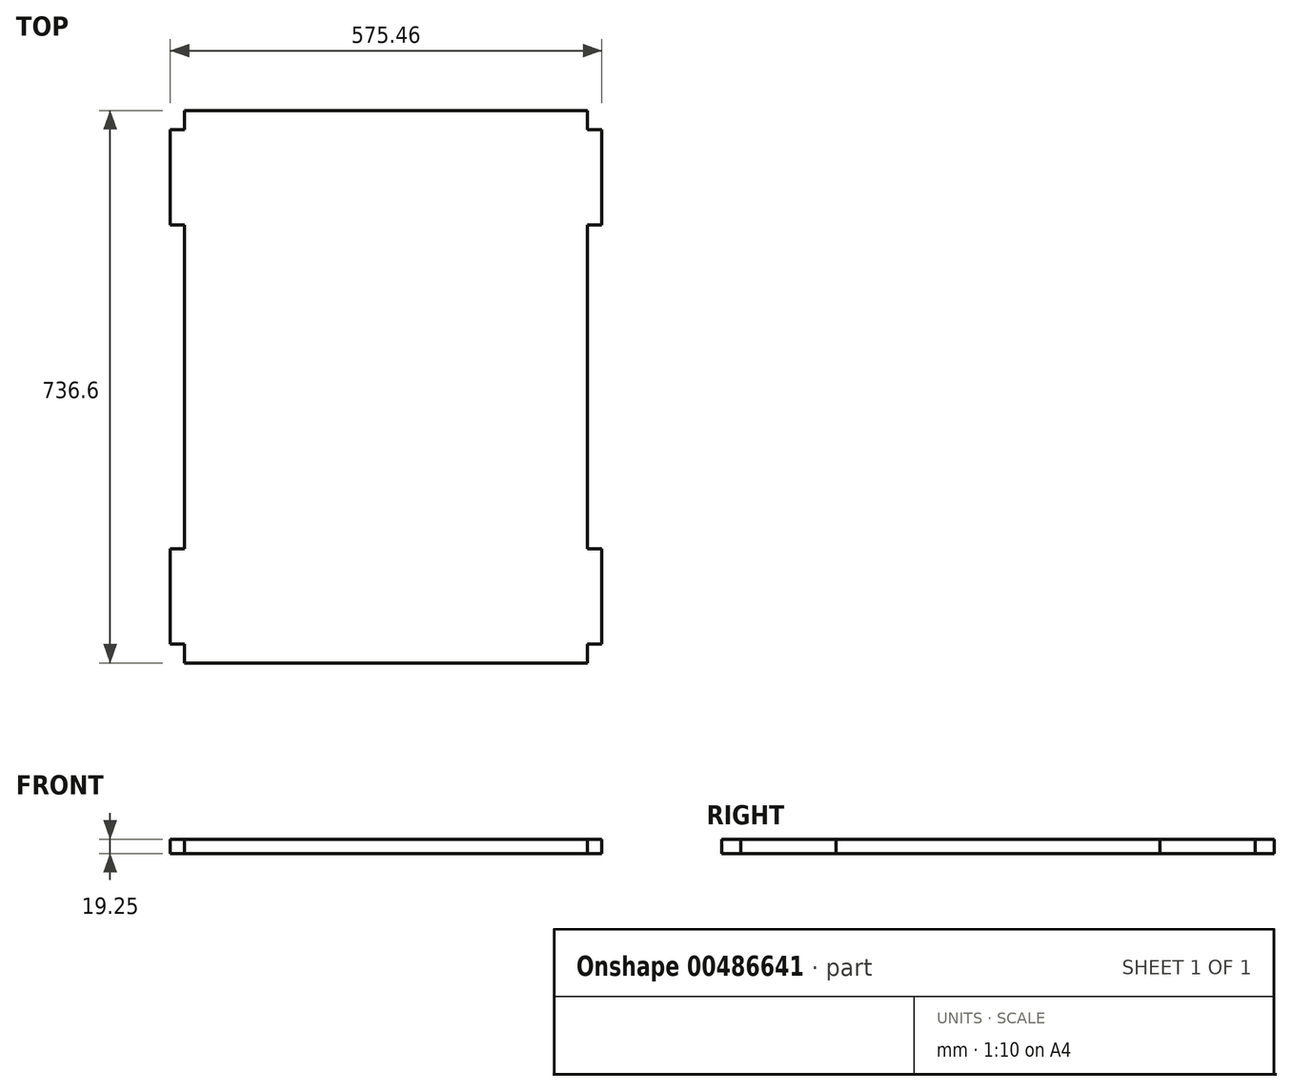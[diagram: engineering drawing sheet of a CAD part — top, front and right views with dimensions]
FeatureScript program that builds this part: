
annotation { "Feature Type Name" : "Feature", "Feature Type Description" : "" }
export const myFeature = defineFeature(function(context is Context, id is Id, definition is map)
    precondition{}
    {
        {
            var Q0;
            Q0=qCreatedBy(makeId("Top.planeOp"),FACE);
            var sketch = newSketch(context, id + "F0", { "sketchPlane" : qUnion([Q0])});
            skLineSegment(sketch, "E0.bottom", {"start": v(-533.55, 619.26) * mm, "end": v(3.4, 619.26) * mm});
            skLineSegment(sketch, "E0.top", {"start": v(-533.55, -117.34) * mm, "end": v(3.4, -117.34) * mm});
            skLineSegment(sketch, "E0.left", {"start": v(-533.55, 619.26) * mm, "end": v(-533.55, -117.34) * mm});
            skLineSegment(sketch, "E0.right", {"start": v(3.4, 619.26) * mm, "end": v(3.4, -117.34) * mm});
            skLineSegment(sketch, "E1", {"start": v(-533.55, 593.86) * mm, "end": v(-552.8, 593.86) * mm});
            skLineSegment(sketch, "E2", {"start": v(-552.8, 593.86) * mm, "end": v(-552.8, 466.86) * mm});
            skLineSegment(sketch, "E3", {"start": v(-552.8, 466.86) * mm, "end": v(-533.55, 466.86) * mm});
            skLineSegment(sketch, "E4", {"start": v(-533.55, -91.94) * mm, "end": v(-552.8, -91.94) * mm});
            skLineSegment(sketch, "E5", {"start": v(-552.8, -91.94) * mm, "end": v(-552.8, 35.06) * mm});
            skLineSegment(sketch, "E6", {"start": v(-552.8, 35.06) * mm, "end": v(-533.55, 35.06) * mm});
            skLineSegment(sketch, "E7", {"start": v(3.4, 593.86) * mm, "end": v(22.65, 593.86) * mm});
            skLineSegment(sketch, "E8", {"start": v(22.65, 593.86) * mm, "end": v(22.65, 466.86) * mm});
            skLineSegment(sketch, "E9", {"start": v(22.65, 466.86) * mm, "end": v(3.4, 466.86) * mm});
            skLineSegment(sketch, "E10", {"start": v(3.4, 35.06) * mm, "end": v(22.65, 35.06) * mm});
            skLineSegment(sketch, "E11", {"start": v(22.65, 35.06) * mm, "end": v(22.65, -91.94) * mm});
            skLineSegment(sketch, "E12", {"start": v(22.65, -91.94) * mm, "end": v(3.4, -91.94) * mm});
            skSolve(sketch);
        }
        {
            var Q0;
            Q0 = qSketchRegion(id + "F0", true);
            extrude(context, id + "F1", {"entities" : qUnion([Q0]), "depth" : 19.25 * mm, "offsetDistance" : 25.4 * mm});
        }
    });
